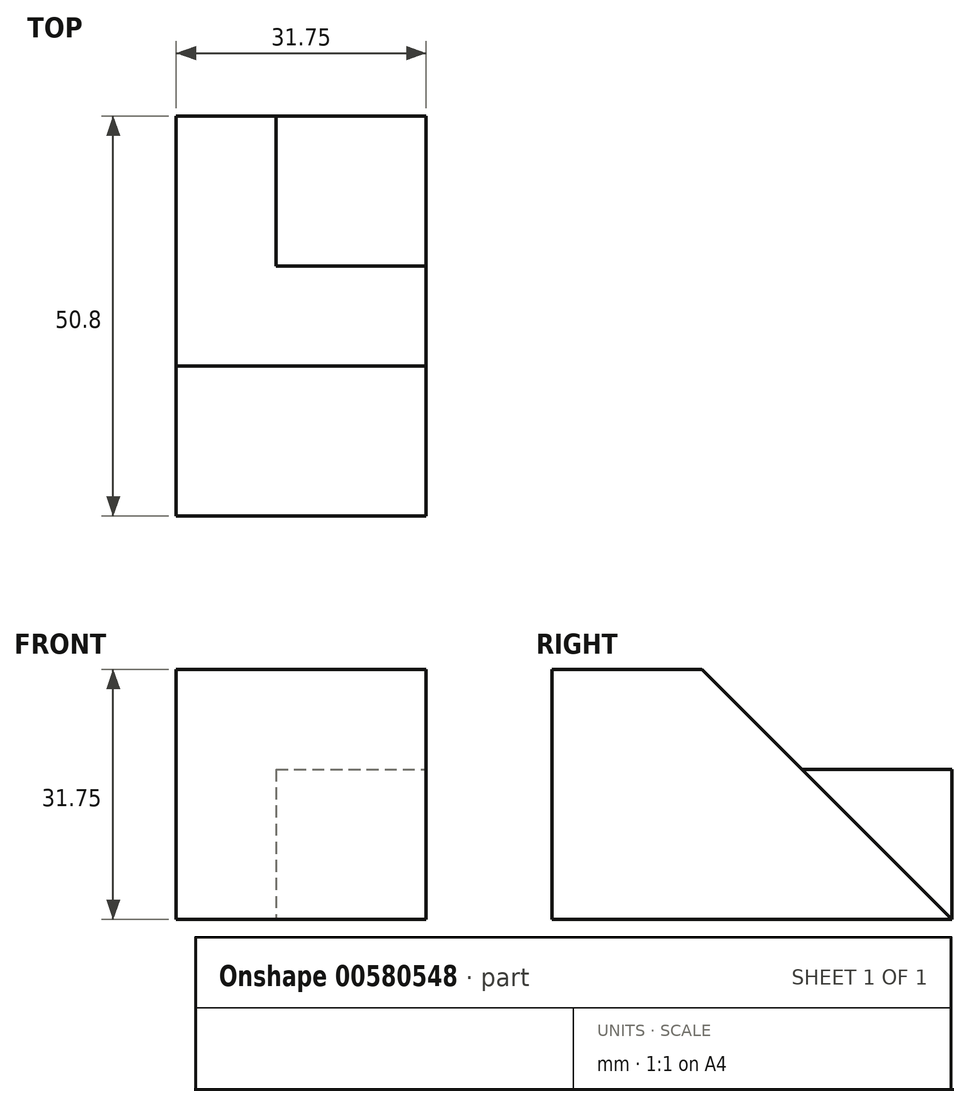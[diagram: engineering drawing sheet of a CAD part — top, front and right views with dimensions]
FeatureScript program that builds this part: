
annotation { "Feature Type Name" : "Feature", "Feature Type Description" : "" }
export const myFeature = defineFeature(function(context is Context, id is Id, definition is map)
    precondition{}
    {
        {
            var Q0;
            Q0=qCreatedBy(makeId("Right.planeOp"),FACE);
            var sketch = newSketch(context, id + "F0", { "sketchPlane" : qUnion([Q0])});
            skLineSegment(sketch, "E0", {"start": v(61.71, 63.6) * mm, "end": v(61.71, 31.85) * mm});
            skLineSegment(sketch, "E1", {"start": v(61.71, 31.85) * mm, "end": v(10.91, 31.85) * mm});
            skLineSegment(sketch, "E2", {"start": v(10.91, 31.85) * mm, "end": v(10.91, 63.6) * mm});
            skLineSegment(sketch, "E3", {"start": v(10.91, 63.6) * mm, "end": v(61.71, 63.6) * mm});
            skSolve(sketch);
        }
        {
            var Q0;
            Q0 = qSketchRegion(id + "F0", true);
            extrude(context, id + "F1", {"entities" : qUnion([Q0]), "depth" : 31.75 * mm, "offsetDistance" : 25.4 * mm});
        }
        {
            var Q0;
            Q0=makeQuery(id+"F1.opExtrude","CAP_FACE",FACE,{"disambiguationData":[OSD([sQuery(id+"F0.wireOp",EDGE,"E0"),sQuery(id+"F0.wireOp",EDGE,"E1"),sQuery(id+"F0.wireOp",EDGE,"E2"),sQuery(id+"F0.wireOp",EDGE,"E3")])],"isStart":false});
            var sketch = newSketch(context, id + "F2", { "sketchPlane" : qUnion([Q0])});
            skLineSegment(sketch, "E4", {"start": v(29.96, 63.6) * mm, "end": v(61.71, 31.85) * mm});
            skLineSegment(sketch, "E5", {"start": v(61.71, 31.85) * mm, "end": v(61.71, 63.6) * mm});
            skLineSegment(sketch, "E6", {"start": v(61.71, 63.6) * mm, "end": v(29.96, 63.6) * mm});
            skSolve(sketch);
        }
        {
            var Q0;
            Q0 = qSketchRegion(id + "F2", true);
            extrude(context, id + "F3", {"entities" : qUnion([Q0]), "operationType" : NewBodyOperationType.REMOVE, "oppositeDirection" : true, "depth" : 31.75 * mm, "offsetDistance" : 25.4 * mm});
        }
        {
            var Q0;
            Q0=makeQuery(id+"F1.opExtrude","CAP_FACE",FACE,{"disambiguationData":[OSD([sQuery(id+"F0.wireOp",EDGE,"E0"),sQuery(id+"F0.wireOp",EDGE,"E1"),sQuery(id+"F0.wireOp",EDGE,"E2"),sQuery(id+"F0.wireOp",EDGE,"E3")])],"isStart":false});
            var sketch = newSketch(context, id + "F4", { "sketchPlane" : qUnion([Q0])});
            skLineSegment(sketch, "E7", {"start": v(42.66, 50.9) * mm, "end": v(61.71, 50.9) * mm});
            skLineSegment(sketch, "E8", {"start": v(61.71, 50.9) * mm, "end": v(61.71, 31.85) * mm});
            skLineSegment(sketch, "E9", {"start": v(61.71, 31.85) * mm, "end": v(42.66, 50.9) * mm});
            skSolve(sketch);
        }
        {
            var Q0;
            Q0 = qSketchRegion(id + "F4", true);
            extrude(context, id + "F5", {"entities" : qUnion([Q0]), "oppositeDirection" : true, "depth" : 19.05 * mm, "offsetDistance" : 25.4 * mm});
        }
    });
